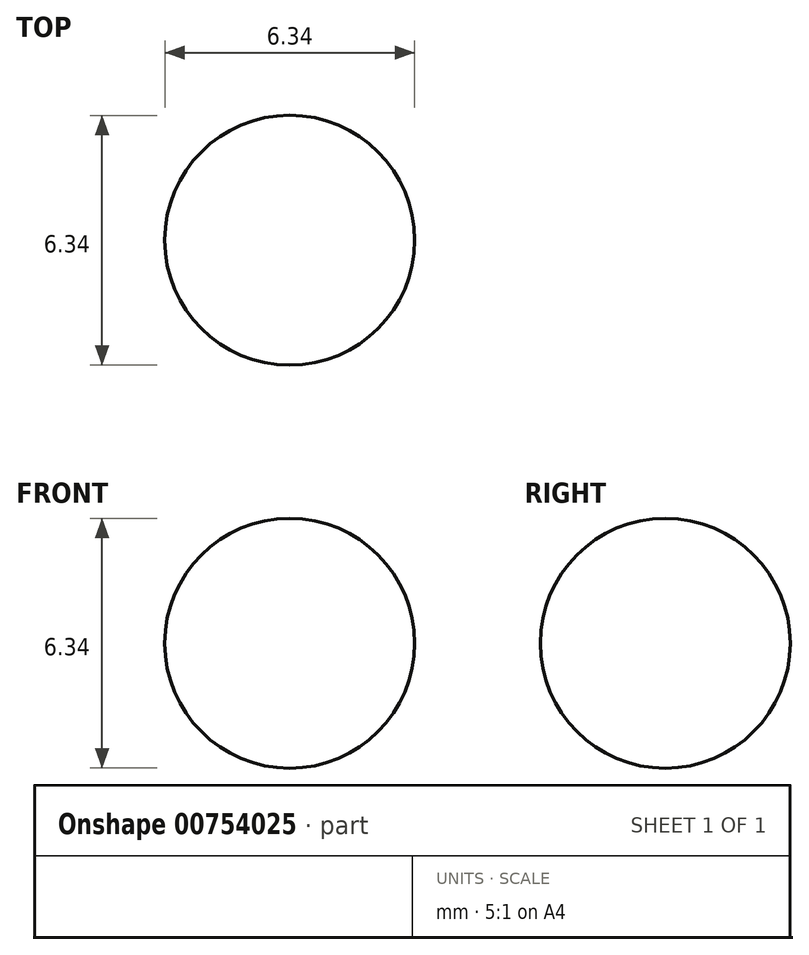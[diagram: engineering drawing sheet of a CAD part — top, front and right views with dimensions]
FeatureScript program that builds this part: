
annotation { "Feature Type Name" : "Feature", "Feature Type Description" : "" }
export const myFeature = defineFeature(function(context is Context, id is Id, definition is map)
    precondition{}
    {
        {
            var Q0;
            Q0=qCreatedBy(makeId("Front.planeOp"),FACE);
            var sketch = newSketch(context, id + "F0", { "sketchPlane" : qUnion([Q0])});
            skArc(sketch, "E0", {"start": v(0, -3.17) * mm, "mid": v(3.17, 0) * mm, "end": v(0, 3.17) * mm});
            skLineSegment(sketch, "E1", {"start": v(0, 3.17) * mm, "end": v(0, -3.17) * mm});
            skLineSegment(sketch, "E2", {"start": v(0, -3.17) * mm, "end": v(0, -6.92) * mm, "construction": true});
            skSolve(sketch);
        }
        {
            var Q0;
            Q0=qSketchRegion(id+"F0",true);
            var Q1;
            Q1=sQuery(id+"F0.wireOp",EDGE,"E2");
            revolve(context, id + "F1", {"entities" : qUnion([Q0]), "axis" : qUnion([Q1]), "revolveType" : RevolveType.FULL});
        }
    });
